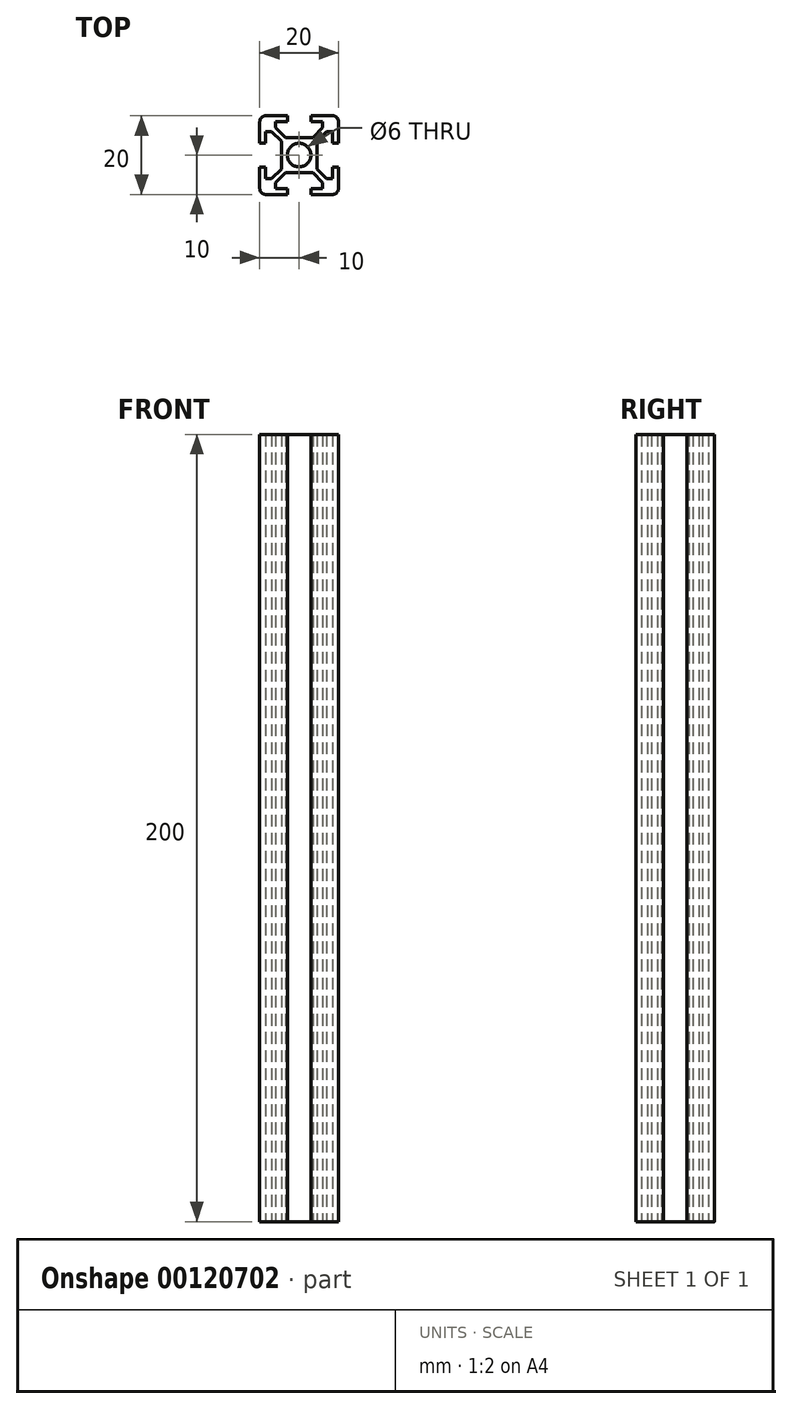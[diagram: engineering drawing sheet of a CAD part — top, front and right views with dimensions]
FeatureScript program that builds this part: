
annotation { "Feature Type Name" : "Feature", "Feature Type Description" : "" }
export const myFeature = defineFeature(function(context is Context, id is Id, definition is map)
    precondition{}
    {
        {
            var Q0;
            Q0=qCreatedBy(makeId("Top.planeOp"),FACE);
            var sketch = newSketch(context, id + "F0", { "sketchPlane" : qUnion([Q0])});
            skLineSegment(sketch, "E0.bottom", {"start": v(1.5, 0) * mm, "end": v(7, 0) * mm});
            skLineSegment(sketch, "E0.top", {"start": v(1.5, 20) * mm, "end": v(7, 20) * mm});
            skLineSegment(sketch, "E0.left", {"start": v(0, 1.5) * mm, "end": v(0, 7) * mm});
            skLineSegment(sketch, "E0.right", {"start": v(20, 1.5) * mm, "end": v(20, 7) * mm});
            skLineSegment(sketch, "E1", {"start": v(10, 25.59) * mm, "end": v(10, -6.26) * mm, "construction": true});
            skPoint(sketch, "E1.startSnap0", {"position": v(10, 20) * mm});
            skLineSegment(sketch, "E2", {"start": v(-5.38, 10) * mm, "end": v(26.16, 10) * mm, "construction": true});
            skPoint(sketch, "E2.startSnap0", {"position": v(0, 10) * mm});
            skPoint(sketch, "E3.visualSharp", {"position": v(20, 20) * mm});
            skArc(sketch, "E3.filletArc", {"start": v(20, 18.5) * mm, "mid": v(19.56, 19.56) * mm, "end": v(18.5, 20) * mm});
            skPoint(sketch, "E4.visualSharp", {"position": v(20, 0) * mm});
            skArc(sketch, "E4.filletArc", {"start": v(18.5, 0) * mm, "mid": v(19.56, 0.44) * mm, "end": v(20, 1.5) * mm});
            skPoint(sketch, "E5.visualSharp", {"position": v(0, 0) * mm});
            skArc(sketch, "E5.filletArc", {"start": v(0, 1.5) * mm, "mid": v(0.44, 0.44) * mm, "end": v(1.5, 0) * mm});
            skPoint(sketch, "E6.visualSharp", {"position": v(0, 20) * mm});
            skArc(sketch, "E6.filletArc", {"start": v(1.5, 20) * mm, "mid": v(0.44, 19.56) * mm, "end": v(0, 18.5) * mm});
            skLineSegment(sketch, "E7", {"start": v(20, 13) * mm, "end": v(18.5, 13) * mm});
            skLineSegment(sketch, "E8", {"start": v(18.5, 13) * mm, "end": v(18.5, 16) * mm});
            skLineSegment(sketch, "E9", {"start": v(18.5, 16) * mm, "end": v(17, 16) * mm});
            skLineSegment(sketch, "E10", {"start": v(17, 16) * mm, "end": v(14.5, 13.5) * mm});
            skLineSegment(sketch, "E11", {"start": v(14.5, 13.5) * mm, "end": v(14.5, 10) * mm});
            skLineSegment(sketch, "E12.MirrorCS", {"start": v(20, 7) * mm, "end": v(18.5, 7) * mm});
            skLineSegment(sketch, "E13.MirrorCS", {"start": v(18.5, 7) * mm, "end": v(18.5, 4) * mm});
            skLineSegment(sketch, "E14.MirrorCS", {"start": v(18.5, 4) * mm, "end": v(17, 4) * mm});
            skLineSegment(sketch, "E15.MirrorCS", {"start": v(14.5, 6.5) * mm, "end": v(14.5, 10) * mm});
            skLineSegment(sketch, "E16.MirrorCS", {"start": v(17, 4) * mm, "end": v(14.5, 6.5) * mm});
            skLineSegment(sketch, "E17.MirrorCS", {"start": v(0, 13) * mm, "end": v(1.5, 13) * mm});
            skLineSegment(sketch, "E18.MirrorCS", {"start": v(1.5, 13) * mm, "end": v(1.5, 16) * mm});
            skLineSegment(sketch, "E19.MirrorCS", {"start": v(1.5, 16) * mm, "end": v(3, 16) * mm});
            skLineSegment(sketch, "E20.MirrorCS", {"start": v(3, 16) * mm, "end": v(5.5, 13.5) * mm});
            skLineSegment(sketch, "E21.MirrorCS", {"start": v(5.5, 13.5) * mm, "end": v(5.5, 10) * mm});
            skLineSegment(sketch, "E22.MirrorCS", {"start": v(5.5, 6.5) * mm, "end": v(5.5, 10) * mm});
            skLineSegment(sketch, "E23.MirrorCS", {"start": v(3, 4) * mm, "end": v(5.5, 6.5) * mm});
            skLineSegment(sketch, "E24.MirrorCS", {"start": v(1.5, 4) * mm, "end": v(3, 4) * mm});
            skLineSegment(sketch, "E25.MirrorCS", {"start": v(1.5, 7) * mm, "end": v(1.5, 4) * mm});
            skLineSegment(sketch, "E26.MirrorCS", {"start": v(0, 7) * mm, "end": v(1.5, 7) * mm});
            skLineSegment(sketch, "E27.1.0", {"start": v(13, 20) * mm, "end": v(13, 18.5) * mm});
            skLineSegment(sketch, "E27.1.1", {"start": v(13, 18.5) * mm, "end": v(16, 18.5) * mm});
            skLineSegment(sketch, "E27.1.2", {"start": v(16, 18.5) * mm, "end": v(16, 17) * mm});
            skLineSegment(sketch, "E27.1.3", {"start": v(16, 17) * mm, "end": v(13.5, 14.5) * mm});
            skLineSegment(sketch, "E27.1.4", {"start": v(13.5, 14.5) * mm, "end": v(10, 14.5) * mm});
            skLineSegment(sketch, "E27.1.5", {"start": v(6.5, 14.5) * mm, "end": v(10, 14.5) * mm});
            skLineSegment(sketch, "E27.1.6", {"start": v(4, 17) * mm, "end": v(6.5, 14.5) * mm});
            skLineSegment(sketch, "E27.1.7", {"start": v(4, 18.5) * mm, "end": v(4, 17) * mm});
            skLineSegment(sketch, "E27.1.8", {"start": v(7, 18.5) * mm, "end": v(4, 18.5) * mm});
            skLineSegment(sketch, "E27.1.9", {"start": v(7, 20) * mm, "end": v(7, 18.5) * mm});
            skPoint(sketch, "E27.center", {"position": v(10, 10) * mm});
            skLineSegment(sketch, "E27.anchor1", {"start": v(10, 10) * mm, "end": v(0, 13) * mm, "construction": true});
            skLineSegment(sketch, "E27.anchor2", {"start": v(10, 10) * mm, "end": v(13, 20) * mm, "construction": true});
            skLineSegment(sketch, "E28.MirrorCS", {"start": v(7, 0) * mm, "end": v(7, 1.5) * mm});
            skLineSegment(sketch, "E29.MirrorCS", {"start": v(7, 1.5) * mm, "end": v(4, 1.5) * mm});
            skLineSegment(sketch, "E30.MirrorCS", {"start": v(4, 1.5) * mm, "end": v(4, 3) * mm});
            skLineSegment(sketch, "E31.MirrorCS", {"start": v(4, 3) * mm, "end": v(6.5, 5.5) * mm});
            skLineSegment(sketch, "E32.MirrorCS", {"start": v(6.5, 5.5) * mm, "end": v(10, 5.5) * mm});
            skLineSegment(sketch, "E33.MirrorCS", {"start": v(13.5, 5.5) * mm, "end": v(10, 5.5) * mm});
            skLineSegment(sketch, "E34.MirrorCS", {"start": v(16, 3) * mm, "end": v(13.5, 5.5) * mm});
            skLineSegment(sketch, "E35.MirrorCS", {"start": v(16, 1.5) * mm, "end": v(16, 3) * mm});
            skLineSegment(sketch, "E36.MirrorCS", {"start": v(13, 1.5) * mm, "end": v(16, 1.5) * mm});
            skLineSegment(sketch, "E37.MirrorCS", {"start": v(13, 0) * mm, "end": v(13, 1.5) * mm});
            skLineSegment(sketch, "E38.trimOffspring", {"start": v(13, 20) * mm, "end": v(18.5, 20) * mm});
            skLineSegment(sketch, "E39.trimOffspring", {"start": v(20, 13) * mm, "end": v(20, 18.5) * mm});
            skLineSegment(sketch, "E40.trimOffspring", {"start": v(13, 0) * mm, "end": v(18.5, 0) * mm});
            skLineSegment(sketch, "E41.trimOffspring", {"start": v(0, 13) * mm, "end": v(0, 18.5) * mm});
            skCircle(sketch, "E42", {"center": v(10, 10) * mm, "radius": 3 * mm});
            skSolve(sketch);
        }
        {
            var Q0;
            Q0=qSketchRegion(id+"F0",true);
            extrude(context, id + "F1", {"entities" : qUnion([Q0]), "depth" : 200 * mm});
        }
    });
